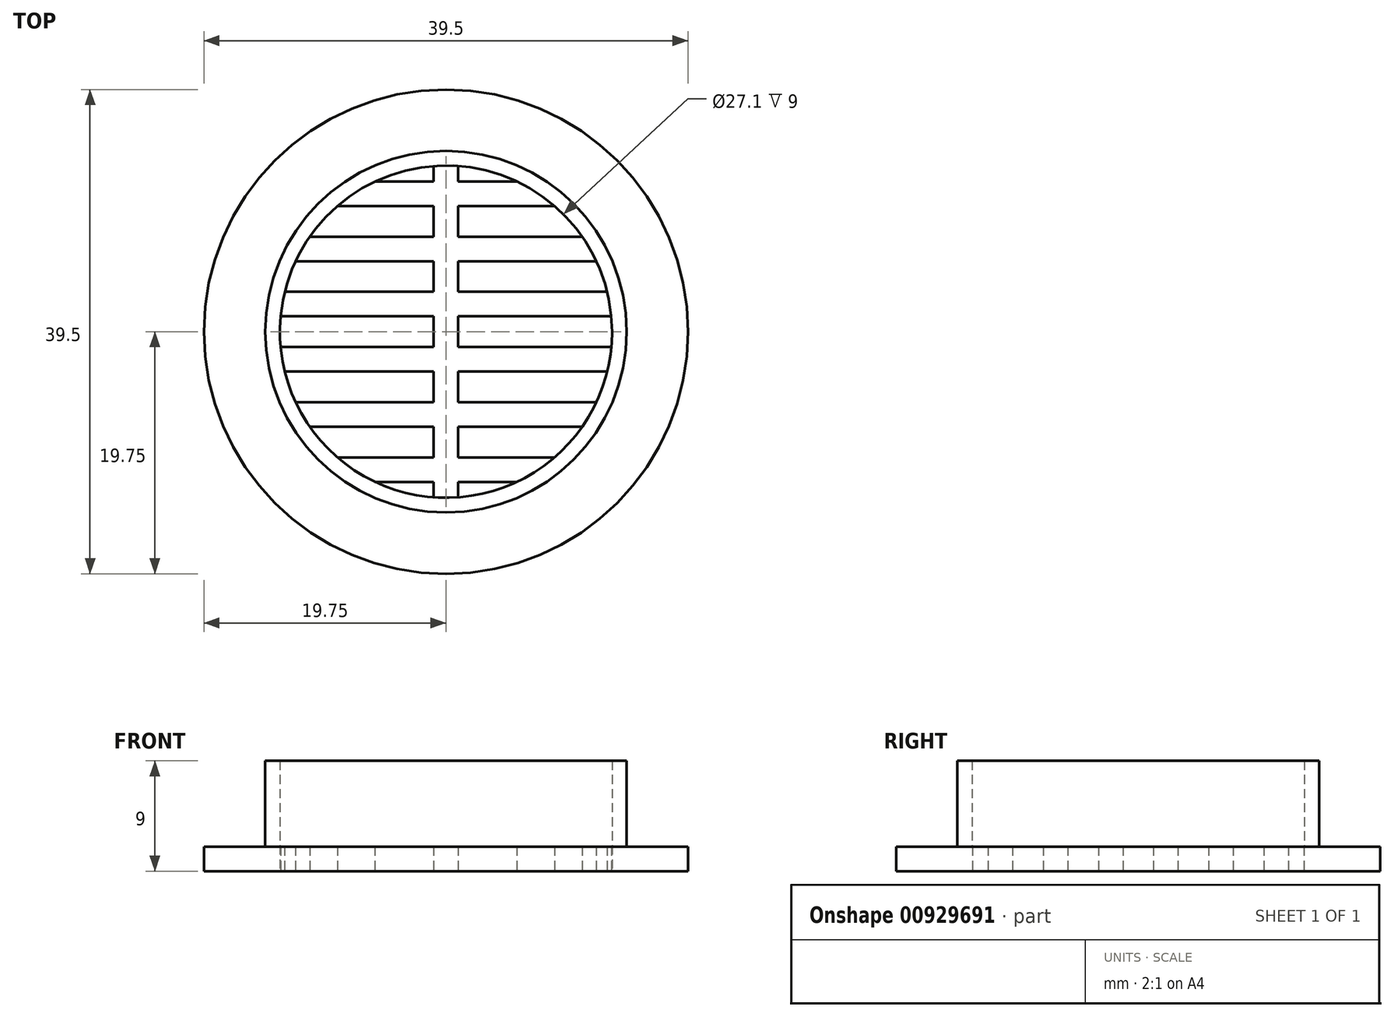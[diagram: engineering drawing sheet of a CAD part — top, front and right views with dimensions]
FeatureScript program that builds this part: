
annotation { "Feature Type Name" : "Feature", "Feature Type Description" : "" }
export const myFeature = defineFeature(function(context is Context, id is Id, definition is map)
    precondition{}
    {
        {
            var Q0;
            Q0=qCreatedBy(makeId("Top.planeOp"),FACE);
            var sketch = newSketch(context, id + "F0", { "sketchPlane" : qUnion([Q0])});
            skCircle(sketch, "E0", {"center": v(0, 0) * mm, "radius": 14.75 * mm, "construction": true});
            skCircle(sketch, "E1", {"center": v(0, 0) * mm, "radius": 19.75 * mm});
            skLineSegment(sketch, "E2", {"start": v(14.75, 0) * mm, "end": v(19.75, 0) * mm, "construction": true});
            skSolve(sketch);
        }
        {
            var Q0;
            Q0 = qSketchRegion(id + "F0", true);
            extrude(context, id + "F1", {"entities" : qUnion([Q0]), "depth" : 2 * mm, "offsetDistance" : 25 * mm});
        }
        {
            var Q0;
            Q0=qCreatedBy(makeId("Front.planeOp"),FACE);
            var sketch = newSketch(context, id + "F2", { "sketchPlane" : qUnion([Q0])});
            skLineSegment(sketch, "E3", {"start": v(0, 0) * mm, "end": v(0, 24.06) * mm, "construction": true});
            skSolve(sketch);
        }
        {
            var Q0;
            Q0=makeQuery(id+"F1.opExtrude","CAP_FACE",FACE,{"disambiguationData":[OSD([sQuery(id+"F0.wireOp",EDGE,"E1")])],"isStart":false});
            var sketch = newSketch(context, id + "F3", { "sketchPlane" : qUnion([Q0])});
            skLineSegment(sketch, "E4.bottom", {"start": v(-14.75, -14.75) * mm, "end": v(14.75, -14.75) * mm});
            skLineSegment(sketch, "E4.top", {"start": v(-14.75, -16.75) * mm, "end": v(14.75, -16.75) * mm});
            skLineSegment(sketch, "E4.left", {"start": v(-14.75, -14.75) * mm, "end": v(-14.75, -16.75) * mm});
            skLineSegment(sketch, "E4.right", {"start": v(14.75, -14.75) * mm, "end": v(14.75, -16.75) * mm});
            skPoint(sketch, "E5", {"position": v(-14.75, -15.75) * mm});
            skCircle(sketch, "E6.0", {"center": v(0, 0) * mm, "radius": 14.75 * mm, "construction": true});
            skLineSegment(sketch, "E7", {"start": v(-14.75, 0) * mm, "end": v(14.75, 0) * mm, "construction": true});
            skLineSegment(sketch, "E8.1.0.0", {"start": v(-14.75, -10.25) * mm, "end": v(14.75, -10.25) * mm});
            skLineSegment(sketch, "E8.1.0.1", {"start": v(-14.75, -10.25) * mm, "end": v(-14.75, -12.25) * mm});
            skLineSegment(sketch, "E8.1.0.2", {"start": v(-14.75, -12.25) * mm, "end": v(14.75, -12.25) * mm});
            skLineSegment(sketch, "E8.1.0.3", {"start": v(14.75, -10.25) * mm, "end": v(14.75, -12.25) * mm});
            skLineSegment(sketch, "E8.2.0.0", {"start": v(-14.75, -5.75) * mm, "end": v(14.75, -5.75) * mm});
            skLineSegment(sketch, "E8.2.0.1", {"start": v(-14.75, -5.75) * mm, "end": v(-14.75, -7.75) * mm});
            skLineSegment(sketch, "E8.2.0.2", {"start": v(-14.75, -7.75) * mm, "end": v(14.75, -7.75) * mm});
            skLineSegment(sketch, "E8.2.0.3", {"start": v(14.75, -5.75) * mm, "end": v(14.75, -7.75) * mm});
            skLineSegment(sketch, "E8.direction1", {"start": v(-14.75, -16.75) * mm, "end": v(-14.75, -12.25) * mm, "construction": true});
            skLineSegment(sketch, "E9.0.3.0", {"start": v(-14.75, -1.25) * mm, "end": v(14.75, -1.25) * mm});
            skLineSegment(sketch, "E9.3.3.0", {"start": v(-14.75, -1.25) * mm, "end": v(-14.75, -3.25) * mm});
            skLineSegment(sketch, "E9.6.3.0", {"start": v(-14.75, -3.25) * mm, "end": v(14.75, -3.25) * mm});
            skLineSegment(sketch, "E9.9.3.0", {"start": v(14.75, -1.25) * mm, "end": v(14.75, -3.25) * mm});
            skLineSegment(sketch, "E9.0.4.0", {"start": v(-14.75, 3.25) * mm, "end": v(14.75, 3.25) * mm});
            skLineSegment(sketch, "E9.3.4.0", {"start": v(-14.75, 3.25) * mm, "end": v(-14.75, 1.25) * mm});
            skLineSegment(sketch, "E9.6.4.0", {"start": v(-14.75, 1.25) * mm, "end": v(14.75, 1.25) * mm});
            skLineSegment(sketch, "E9.9.4.0", {"start": v(14.75, 3.25) * mm, "end": v(14.75, 1.25) * mm});
            skLineSegment(sketch, "E9.0.5.0", {"start": v(-14.75, 7.75) * mm, "end": v(14.75, 7.75) * mm});
            skLineSegment(sketch, "E9.3.5.0", {"start": v(-14.75, 7.75) * mm, "end": v(-14.75, 5.75) * mm});
            skLineSegment(sketch, "E9.6.5.0", {"start": v(-14.75, 5.75) * mm, "end": v(14.75, 5.75) * mm});
            skLineSegment(sketch, "E9.9.5.0", {"start": v(14.75, 7.75) * mm, "end": v(14.75, 5.75) * mm});
            skLineSegment(sketch, "E10.0.6.0", {"start": v(-14.75, 12.25) * mm, "end": v(14.75, 12.25) * mm});
            skLineSegment(sketch, "E10.3.6.0", {"start": v(-14.75, 12.25) * mm, "end": v(-14.75, 10.25) * mm});
            skLineSegment(sketch, "E10.6.6.0", {"start": v(-14.75, 10.25) * mm, "end": v(14.75, 10.25) * mm});
            skLineSegment(sketch, "E10.9.6.0", {"start": v(14.75, 12.25) * mm, "end": v(14.75, 10.25) * mm});
            skLineSegment(sketch, "E11.0.7.0", {"start": v(-14.75, 16.75) * mm, "end": v(14.75, 16.75) * mm});
            skLineSegment(sketch, "E11.3.7.0", {"start": v(-14.75, 16.75) * mm, "end": v(-14.75, 14.75) * mm});
            skLineSegment(sketch, "E11.6.7.0", {"start": v(-14.75, 14.75) * mm, "end": v(14.75, 14.75) * mm});
            skLineSegment(sketch, "E11.9.7.0", {"start": v(14.75, 16.75) * mm, "end": v(14.75, 14.75) * mm});
            skPoint(sketch, "E12", {"position": v(0, 14.75) * mm});
            skPoint(sketch, "E13", {"position": v(0, -14.75) * mm});
            skPoint(sketch, "E13.positionSnap0", {"position": v(0, -12.25) * mm});
            skSolve(sketch);
        }
        {
            var Q0;
            Q0 = qSketchRegion(id + "F3", true);
            var Q1;
            Q1=makeQuery(id+"F1.opExtrude","CAP_FACE",FACE,{"disambiguationData":[OSD([sQuery(id+"F0.wireOp",EDGE,"E1")])],"isStart":true});
            extrude(context, id + "F4", {"entities" : qUnion([Q0]), "endBound" : BoundingType.UP_TO_SURFACE, "oppositeDirection" : true, "depth" : 25 * mm, "endBoundEntityFace" : qUnion([Q1]), "offsetDistance" : 25 * mm});
        }
        {
            var Q0;
            Q0=qCreatedBy(makeId("Top.planeOp"),FACE);
            var sketch = newSketch(context, id + "F5", { "sketchPlane" : qUnion([Q0])});
            skCircle(sketch, "E14.0", {"center": v(0, 0) * mm, "radius": 14.75 * mm});
            skSolve(sketch);
        }
        {
            var Q0;
            Q0 = qSketchRegion(id + "F5", true);
            var Q1;
            Q1=makeQuery(id+"F1.opExtrude","CAP_FACE",FACE,{"disambiguationData":[OSD([sQuery(id+"F0.wireOp",EDGE,"E1")])],"isStart":false});
            extrude(context, id + "F6", {"entities" : qUnion([Q0]), "endBound" : BoundingType.UP_TO_SURFACE, "depth" : 25 * mm, "endBoundEntityFace" : qUnion([Q1]), "offsetDistance" : 25 * mm});
        }
        {
            var Q0;
            Q0=makeQuery(id+"F4.opExtrude","SWEPT_BODY",BODY,{"disambiguationData":[OSD([sQuery(id+"F3.wireOp",EDGE,"E11.0.7.0"),sQuery(id+"F3.wireOp",EDGE,"E11.3.7.0"),sQuery(id+"F3.wireOp",EDGE,"E11.6.7.0"),sQuery(id+"F3.wireOp",EDGE,"E11.9.7.0")])]});
            var Q1;
            Q1=makeQuery(id+"F4.opExtrude","SWEPT_BODY",BODY,{"disambiguationData":[OSD([sQuery(id+"F3.wireOp",EDGE,"E10.0.6.0"),sQuery(id+"F3.wireOp",EDGE,"E10.3.6.0"),sQuery(id+"F3.wireOp",EDGE,"E10.6.6.0"),sQuery(id+"F3.wireOp",EDGE,"E10.9.6.0")])]});
            var Q2;
            Q2=makeQuery(id+"F4.opExtrude","SWEPT_BODY",BODY,{"disambiguationData":[OSD([sQuery(id+"F3.wireOp",EDGE,"E9.0.5.0"),sQuery(id+"F3.wireOp",EDGE,"E9.3.5.0"),sQuery(id+"F3.wireOp",EDGE,"E9.6.5.0"),sQuery(id+"F3.wireOp",EDGE,"E9.9.5.0")])]});
            var Q3;
            Q3=makeQuery(id+"F4.opExtrude","SWEPT_BODY",BODY,{"disambiguationData":[OSD([sQuery(id+"F3.wireOp",EDGE,"E9.0.4.0"),sQuery(id+"F3.wireOp",EDGE,"E9.3.4.0"),sQuery(id+"F3.wireOp",EDGE,"E9.6.4.0"),sQuery(id+"F3.wireOp",EDGE,"E9.9.4.0")])]});
            var Q4;
            Q4=makeQuery(id+"F4.opExtrude","SWEPT_BODY",BODY,{"disambiguationData":[OSD([sQuery(id+"F3.wireOp",EDGE,"E9.0.3.0"),sQuery(id+"F3.wireOp",EDGE,"E9.3.3.0"),sQuery(id+"F3.wireOp",EDGE,"E9.6.3.0"),sQuery(id+"F3.wireOp",EDGE,"E9.9.3.0")])]});
            var Q5;
            Q5=makeQuery(id+"F4.opExtrude","SWEPT_BODY",BODY,{"disambiguationData":[OSD([sQuery(id+"F3.wireOp",EDGE,"E8.2.0.0"),sQuery(id+"F3.wireOp",EDGE,"E8.2.0.1"),sQuery(id+"F3.wireOp",EDGE,"E8.2.0.2"),sQuery(id+"F3.wireOp",EDGE,"E8.2.0.3")])]});
            var Q6;
            Q6=makeQuery(id+"F4.opExtrude","SWEPT_BODY",BODY,{"disambiguationData":[OSD([sQuery(id+"F3.wireOp",EDGE,"E8.1.0.0"),sQuery(id+"F3.wireOp",EDGE,"E8.1.0.1"),sQuery(id+"F3.wireOp",EDGE,"E8.1.0.2"),sQuery(id+"F3.wireOp",EDGE,"E8.1.0.3")])]});
            var Q7;
            Q7=makeQuery(id+"F4.opExtrude","SWEPT_BODY",BODY,{"disambiguationData":[OSD([sQuery(id+"F3.wireOp",EDGE,"E4.bottom"),sQuery(id+"F3.wireOp",EDGE,"E4.top"),sQuery(id+"F3.wireOp",EDGE,"E4.left"),sQuery(id+"F3.wireOp",EDGE,"E4.right")])]});
            var Q8;
            Q8=makeQuery(id+"F6.opExtrude","SWEPT_BODY",BODY,{"disambiguationData":[OSD([sQuery(id+"F5.wireOp",EDGE,"E14.0")])]});
            booleanBodies(context, id + "F7", {"operationType" : BooleanOperationType.SUBTRACTION, "tools" : qUnion([Q0, Q1, Q2, Q3, Q4, Q5, Q6, Q7]), "targets" : qUnion([Q8])});
        }
        {
            var Q0;
            Q0=makeQuery(id+"F7.opBoolean","SPLIT",BODY,{"disambiguationData":[OD(1.0)],"derivedFrom":makeQuery(id+"F6.opExtrude","SWEPT_BODY",BODY,{"disambiguationData":[OSD([sQuery(id+"F5.wireOp",EDGE,"E14.0")])]})});
            var Q1;
            Q1=makeQuery(id+"F7.opBoolean","SPLIT",BODY,{"disambiguationData":[OD(6.0)],"derivedFrom":makeQuery(id+"F6.opExtrude","SWEPT_BODY",BODY,{"disambiguationData":[OSD([sQuery(id+"F5.wireOp",EDGE,"E14.0")])]})});
            var Q2;
            Q2=makeQuery(id+"F7.opBoolean","SPLIT",BODY,{"disambiguationData":[OD(5.0)],"derivedFrom":makeQuery(id+"F6.opExtrude","SWEPT_BODY",BODY,{"disambiguationData":[OSD([sQuery(id+"F5.wireOp",EDGE,"E14.0")])]})});
            var Q3;
            Q3=makeQuery(id+"F7.opBoolean","SPLIT",BODY,{"disambiguationData":[OD(4.0)],"derivedFrom":makeQuery(id+"F6.opExtrude","SWEPT_BODY",BODY,{"disambiguationData":[OSD([sQuery(id+"F5.wireOp",EDGE,"E14.0")])]})});
            var Q4;
            Q4=makeQuery(id+"F7.opBoolean","SPLIT",BODY,{"disambiguationData":[OD(3.0)],"derivedFrom":makeQuery(id+"F6.opExtrude","SWEPT_BODY",BODY,{"disambiguationData":[OSD([sQuery(id+"F5.wireOp",EDGE,"E14.0")])]})});
            var Q5;
            Q5=makeQuery(id+"F7.opBoolean","SPLIT",BODY,{"disambiguationData":[OD(2.0)],"derivedFrom":makeQuery(id+"F6.opExtrude","SWEPT_BODY",BODY,{"disambiguationData":[OSD([sQuery(id+"F5.wireOp",EDGE,"E14.0")])]})});
            var Q6;
            Q6=makeQuery(id+"F7.opBoolean","SPLIT",BODY,{"disambiguationData":[OD(0.0)],"derivedFrom":makeQuery(id+"F6.opExtrude","SWEPT_BODY",BODY,{"disambiguationData":[OSD([sQuery(id+"F5.wireOp",EDGE,"E14.0")])]})});
            var Q7;
            Q7=makeQuery(id+"F1.opExtrude","SWEPT_BODY",BODY,{"disambiguationData":[OSD([sQuery(id+"F0.wireOp",EDGE,"E1")])]});
            booleanBodies(context, id + "F8", {"operationType" : BooleanOperationType.SUBTRACTION, "tools" : qUnion([Q0, Q1, Q2, Q3, Q4, Q5, Q6]), "targets" : qUnion([Q7])});
        }
        {
            var Q0;
            Q0=makeQuery(id+"F0.imprint","IMPRINT",FACE,{"disambiguationData":[TD([[makeQuery(id+"F0.imprint","IMPRINT",EDGE,{"derivedFrom":sQuery(id+"F0.wireOp",EDGE,"E1")}),1.0]])]});
            var sketch = newSketch(context, id + "F9", { "sketchPlane" : qUnion([Q0])});
            skCircle(sketch, "E15.0", {"center": v(0, 0) * mm, "radius": 14.75 * mm});
            skCircle(sketch, "E16", {"center": v(0, 0) * mm, "radius": 13.55 * mm});
            skLineSegment(sketch, "E17", {"start": v(13.55, 0) * mm, "end": v(14.75, 0) * mm, "construction": true});
            skSolve(sketch);
        }
        {
            var Q0;
            Q0 = qSketchRegion(id + "F9", true);
            var Q1;
            Q1=makeQuery(id+"F1.opExtrude","CAP_FACE",FACE,{"disambiguationData":[OSD([sQuery(id+"F0.wireOp",EDGE,"E1")])],"isStart":false});
            extrude(context, id + "F10", {"entities" : qUnion([Q0]), "operationType" : NewBodyOperationType.ADD, "endBound" : BoundingType.UP_TO_SURFACE, "depth" : 25 * mm, "endBoundEntityFace" : qUnion([Q1]), "hasOffset" : true, "offsetDistance" : 7 * mm, "offsetOppositeDirection" : true});
        }
        {
            var Q0;
            Q0=makeQuery(id+"F0.imprint","IMPRINT",FACE,{"disambiguationData":[TD([[makeQuery(id+"F0.imprint","IMPRINT",EDGE,{"derivedFrom":sQuery(id+"F0.wireOp",EDGE,"E1")}),1.0]])]});
            var sketch = newSketch(context, id + "F11", { "sketchPlane" : qUnion([Q0])});
            skLineSegment(sketch, "E18.bottom", {"start": v(-1, -16.75) * mm, "end": v(1, -16.75) * mm});
            skLineSegment(sketch, "E18.top", {"start": v(-1, 16.75) * mm, "end": v(1, 16.75) * mm});
            skLineSegment(sketch, "E18.left", {"start": v(-1, -16.75) * mm, "end": v(-1, 16.75) * mm});
            skLineSegment(sketch, "E18.right", {"start": v(1, -16.75) * mm, "end": v(1, 16.75) * mm});
            skCircle(sketch, "E19.0", {"center": v(0, 0) * mm, "radius": 14.75 * mm, "construction": true});
            skPoint(sketch, "E20", {"position": v(0, -14.75) * mm});
            skSolve(sketch);
        }
        {
            var Q0;
            Q0 = qSketchRegion(id + "F11", true);
            var Q1;
            {var subQ0=sQuery(id+"F0.wireOp",EDGE,"E1");Q1=makeQuery(id+"F10.boolean.opBoolean","SPLIT",FACE,{"disambiguationData":[TD([makeQuery(id+"F1.opExtrude","SWEPT_FACE",FACE,{"disambiguationData":[OSD([subQ0])]})])],"derivedFrom":makeQuery(id+"F1.opExtrude","CAP_FACE",FACE,{"disambiguationData":[OSD([subQ0])],"isStart":false})});}
            extrude(context, id + "F12", {"entities" : qUnion([Q0]), "operationType" : NewBodyOperationType.ADD, "endBound" : BoundingType.UP_TO_SURFACE, "depth" : 25 * mm, "endBoundEntityFace" : qUnion([Q1]), "offsetDistance" : 25 * mm});
        }
    });
